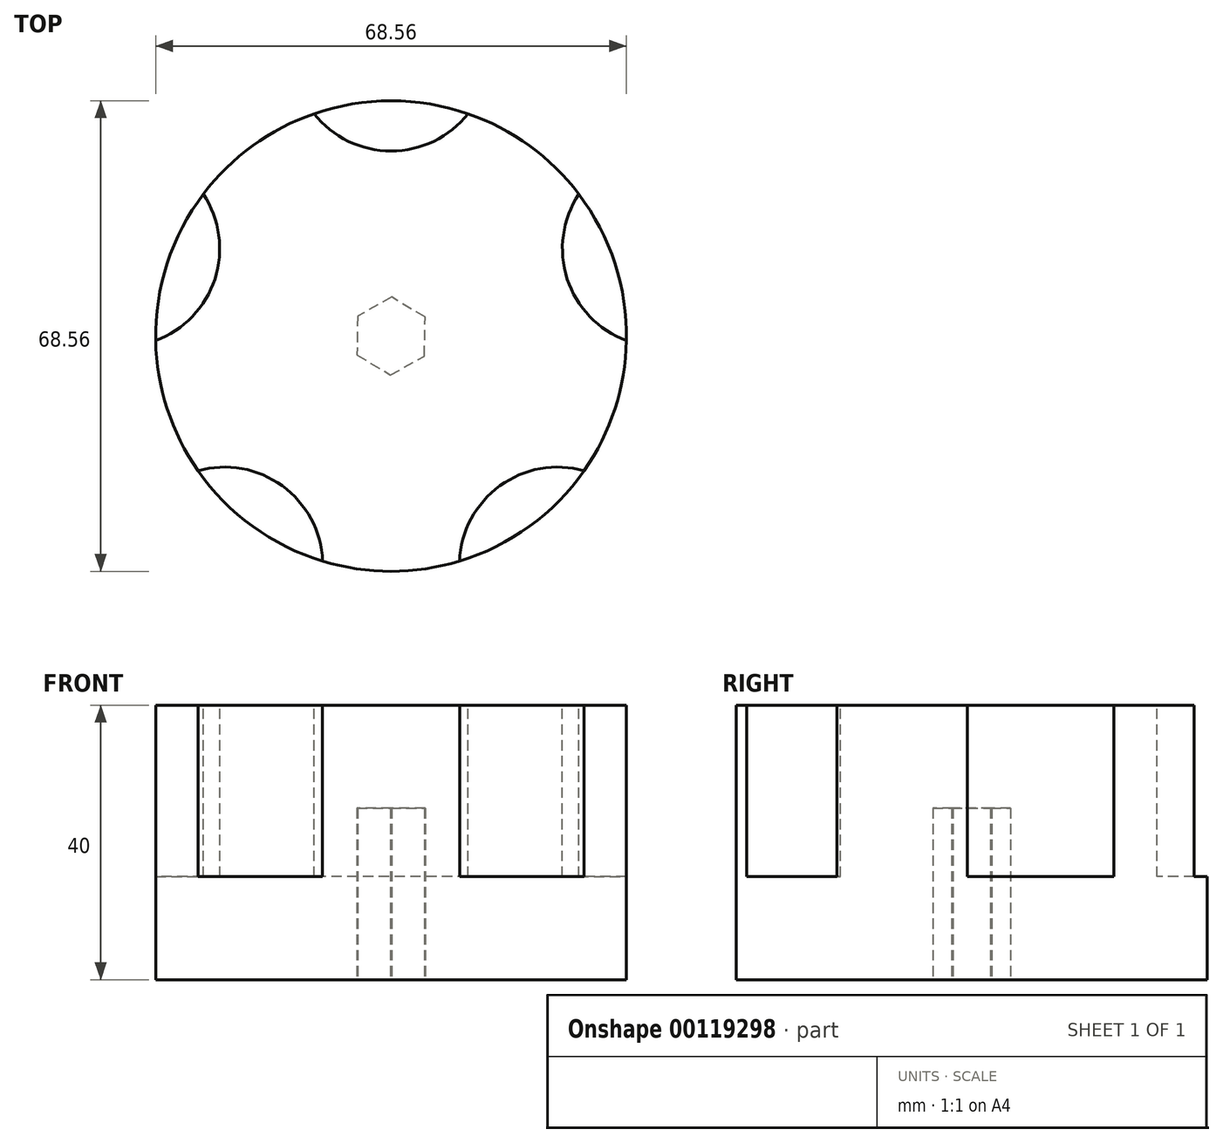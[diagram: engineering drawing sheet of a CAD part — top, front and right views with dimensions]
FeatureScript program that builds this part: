
annotation { "Feature Type Name" : "Feature", "Feature Type Description" : "" }
export const myFeature = defineFeature(function(context is Context, id is Id, definition is map)
    precondition{}
    {
        {
            var Q0;
            Q0=qCreatedBy(makeId("Top.planeOp"),FACE);
            var sketch = newSketch(context, id + "F0", { "sketchPlane" : qUnion([Q0])});
            skCircle(sketch, "E0", {"center": v(-24.43, 29.9) * mm, "radius": 34.28 * mm});
            skSolve(sketch);
        }
        {
            var Q0;
            Q0 = qSketchRegion(id + "F0", true);
            extrude(context, id + "F1", {"entities" : qUnion([Q0]), "depth" : 40 * mm});
        }
        {
            var Q0;
            Q0=makeQuery(id+"F1.opExtrude","CAP_FACE",FACE,{"disambiguationData":[OSD([sQuery(id+"F0.wireOp",EDGE,"E0")])],"isStart":false});
            var sketch = newSketch(context, id + "F2", { "sketchPlane" : qUnion([Q0])});
            skLineSegment(sketch, "E1", {"start": v(-24.43, 29.9) * mm, "end": v(-24.43, 71.17) * mm, "construction": true});
            skCircle(sketch, "E2", {"center": v(-24.43, 71.17) * mm, "radius": 14.3 * mm});
            skCircle(sketch, "E3.1.0", {"center": v(14.83, 42.65) * mm, "radius": 14.3 * mm});
            skCircle(sketch, "E3.2.0", {"center": v(-0.17, -3.49) * mm, "radius": 14.3 * mm});
            skCircle(sketch, "E3.3.0", {"center": v(-48.68, -3.49) * mm, "radius": 14.3 * mm});
            skCircle(sketch, "E3.4.0", {"center": v(-63.68, 42.65) * mm, "radius": 14.3 * mm});
            skPoint(sketch, "E3.center", {"position": v(-24.43, 29.9) * mm});
            skLineSegment(sketch, "E3.anchor2", {"start": v(-24.43, 29.9) * mm, "end": v(-63.68, 42.65) * mm, "construction": true});
            skSolve(sketch);
        }
        {
            var Q0;
            {var subQ0=sQuery(id+"F2.wireOp",EDGE,"E2");var subQ1=makeQuery(id+"F1.opExtrude","CAP_EDGE",EDGE,{"disambiguationData":[OSD([sQuery(id+"F0.wireOp",EDGE,"E0")])],"isStart":false});var subQ2=makeQuery(id+"F2.imprint","INTERSECT",VERTEX,{"disambiguationData":[OD(0.0)],"derivedFrom":[subQ1,subQ0]});Q0=makeQuery(id+"F2.imprint","IMPRINT",FACE,{"disambiguationData":[TD([[makeQuery(id+"F2.imprint","IMPRINT",EDGE,{"disambiguationData":[TD([[subQ2,-1.0]])],"derivedFrom":subQ0}),1.0]])]});}
            var Q1;
            {var subQ0=sQuery(id+"F2.wireOp",EDGE,"E2");var subQ1=makeQuery(id+"F1.opExtrude","CAP_EDGE",EDGE,{"disambiguationData":[OSD([sQuery(id+"F0.wireOp",EDGE,"E0")])],"isStart":false});var subQ2=makeQuery(id+"F2.imprint","INTERSECT",VERTEX,{"disambiguationData":[OD(0.0)],"derivedFrom":[subQ1,subQ0]});Q1=makeQuery(id+"F2.imprint","IMPRINT",FACE,{"disambiguationData":[TD([[makeQuery(id+"F2.imprint","IMPRINT",EDGE,{"disambiguationData":[TD([[subQ2,1.0]])],"derivedFrom":subQ0}),1.0]])]});}
            var Q2;
            {var subQ0=sQuery(id+"F2.wireOp",EDGE,"E3.1.0");var subQ1=makeQuery(id+"F1.opExtrude","CAP_EDGE",EDGE,{"disambiguationData":[OSD([sQuery(id+"F0.wireOp",EDGE,"E0")])],"isStart":false});var subQ2=makeQuery(id+"F2.imprint","INTERSECT",VERTEX,{"disambiguationData":[OD(0.0)],"derivedFrom":[subQ1,subQ0]});Q2=makeQuery(id+"F2.imprint","IMPRINT",FACE,{"disambiguationData":[TD([[makeQuery(id+"F2.imprint","IMPRINT",EDGE,{"disambiguationData":[TD([[subQ2,1.0]])],"derivedFrom":subQ0}),1.0]])]});}
            var Q3;
            {var subQ0=sQuery(id+"F2.wireOp",EDGE,"E3.1.0");var subQ1=makeQuery(id+"F1.opExtrude","CAP_EDGE",EDGE,{"disambiguationData":[OSD([sQuery(id+"F0.wireOp",EDGE,"E0")])],"isStart":false});var subQ2=makeQuery(id+"F2.imprint","INTERSECT",VERTEX,{"disambiguationData":[OD(0.0)],"derivedFrom":[subQ1,subQ0]});Q3=makeQuery(id+"F2.imprint","IMPRINT",FACE,{"disambiguationData":[TD([[makeQuery(id+"F2.imprint","IMPRINT",EDGE,{"disambiguationData":[TD([[subQ2,-1.0]])],"derivedFrom":subQ0}),1.0]])]});}
            var Q4;
            {var subQ0=sQuery(id+"F2.wireOp",EDGE,"E3.2.0");var subQ1=makeQuery(id+"F1.opExtrude","CAP_EDGE",EDGE,{"disambiguationData":[OSD([sQuery(id+"F0.wireOp",EDGE,"E0")])],"isStart":false});var subQ2=makeQuery(id+"F2.imprint","INTERSECT",VERTEX,{"disambiguationData":[OD(0.0)],"derivedFrom":[subQ1,subQ0]});Q4=makeQuery(id+"F2.imprint","IMPRINT",FACE,{"disambiguationData":[TD([[makeQuery(id+"F2.imprint","IMPRINT",EDGE,{"disambiguationData":[TD([[subQ2,1.0]])],"derivedFrom":subQ0}),1.0]])]});}
            var Q5;
            {var subQ0=sQuery(id+"F2.wireOp",EDGE,"E3.2.0");var subQ1=makeQuery(id+"F1.opExtrude","CAP_EDGE",EDGE,{"disambiguationData":[OSD([sQuery(id+"F0.wireOp",EDGE,"E0")])],"isStart":false});var subQ2=makeQuery(id+"F2.imprint","INTERSECT",VERTEX,{"disambiguationData":[OD(0.0)],"derivedFrom":[subQ1,subQ0]});Q5=makeQuery(id+"F2.imprint","IMPRINT",FACE,{"disambiguationData":[TD([[makeQuery(id+"F2.imprint","IMPRINT",EDGE,{"disambiguationData":[TD([[subQ2,-1.0]])],"derivedFrom":subQ0}),1.0]])]});}
            var Q6;
            {var subQ0=sQuery(id+"F2.wireOp",EDGE,"E3.3.0");var subQ1=makeQuery(id+"F1.opExtrude","CAP_EDGE",EDGE,{"disambiguationData":[OSD([sQuery(id+"F0.wireOp",EDGE,"E0")])],"isStart":false});var subQ2=makeQuery(id+"F2.imprint","INTERSECT",VERTEX,{"disambiguationData":[OD(0.0)],"derivedFrom":[subQ1,subQ0]});Q6=makeQuery(id+"F2.imprint","IMPRINT",FACE,{"disambiguationData":[TD([[makeQuery(id+"F2.imprint","IMPRINT",EDGE,{"disambiguationData":[TD([[subQ2,-1.0]])],"derivedFrom":subQ0}),1.0]])]});}
            var Q7;
            {var subQ0=sQuery(id+"F2.wireOp",EDGE,"E3.3.0");var subQ1=makeQuery(id+"F1.opExtrude","CAP_EDGE",EDGE,{"disambiguationData":[OSD([sQuery(id+"F0.wireOp",EDGE,"E0")])],"isStart":false});var subQ2=makeQuery(id+"F2.imprint","INTERSECT",VERTEX,{"disambiguationData":[OD(0.0)],"derivedFrom":[subQ1,subQ0]});Q7=makeQuery(id+"F2.imprint","IMPRINT",FACE,{"disambiguationData":[TD([[makeQuery(id+"F2.imprint","IMPRINT",EDGE,{"disambiguationData":[TD([[subQ2,1.0]])],"derivedFrom":subQ0}),1.0]])]});}
            var Q8;
            {var subQ0=sQuery(id+"F2.wireOp",EDGE,"E3.4.0");var subQ1=makeQuery(id+"F1.opExtrude","CAP_EDGE",EDGE,{"disambiguationData":[OSD([sQuery(id+"F0.wireOp",EDGE,"E0")])],"isStart":false});var subQ2=makeQuery(id+"F2.imprint","INTERSECT",VERTEX,{"disambiguationData":[OD(0.0)],"derivedFrom":[subQ1,subQ0]});Q8=makeQuery(id+"F2.imprint","IMPRINT",FACE,{"disambiguationData":[TD([[makeQuery(id+"F2.imprint","IMPRINT",EDGE,{"disambiguationData":[TD([[subQ2,1.0]])],"derivedFrom":subQ0}),1.0]])]});}
            var Q9;
            {var subQ0=sQuery(id+"F2.wireOp",EDGE,"E3.4.0");var subQ1=makeQuery(id+"F1.opExtrude","CAP_EDGE",EDGE,{"disambiguationData":[OSD([sQuery(id+"F0.wireOp",EDGE,"E0")])],"isStart":false});var subQ2=makeQuery(id+"F2.imprint","INTERSECT",VERTEX,{"disambiguationData":[OD(0.0)],"derivedFrom":[subQ1,subQ0]});Q9=makeQuery(id+"F2.imprint","IMPRINT",FACE,{"disambiguationData":[TD([[makeQuery(id+"F2.imprint","IMPRINT",EDGE,{"disambiguationData":[TD([[subQ2,-1.0]])],"derivedFrom":subQ0}),1.0]])]});}
            extrude(context, id + "F3", {"entities" : qUnion([Q0, Q1, Q2, Q3, Q4, Q5, Q6, Q7, Q8, Q9]), "operationType" : NewBodyOperationType.REMOVE, "oppositeDirection" : true, "depth" : 25 * mm});
        }
        {
            var Q0;
            Q0=makeQuery(id+"F1.opExtrude","CAP_FACE",FACE,{"disambiguationData":[OSD([sQuery(id+"F0.wireOp",EDGE,"E0")])],"isStart":true});
            var sketch = newSketch(context, id + "F4", { "sketchPlane" : qUnion([Q0])});
            skCircle(sketch, "E4.cCircle", {"center": v(-24.43, -29.9) * mm, "radius": 4.91 * mm, "construction": true});
            skLineSegment(sketch, "E4.0", {"start": v(-19.47, -32.65) * mm, "end": v(-24.33, -35.57) * mm});
            skLineSegment(sketch, "E4.1", {"start": v(-24.33, -35.57) * mm, "end": v(-29.29, -32.82) * mm});
            skLineSegment(sketch, "E4.2", {"start": v(-29.29, -32.82) * mm, "end": v(-29.38, -27.15) * mm});
            skLineSegment(sketch, "E4.3", {"start": v(-29.38, -27.15) * mm, "end": v(-24.52, -24.23) * mm});
            skLineSegment(sketch, "E4.4", {"start": v(-24.52, -24.23) * mm, "end": v(-19.56, -26.98) * mm});
            skLineSegment(sketch, "E4.5", {"start": v(-19.56, -26.98) * mm, "end": v(-19.47, -32.65) * mm});
            skPoint(sketch, "E4.0.midPoint", {"position": v(-21.9, -34.11) * mm});
            skSolve(sketch);
        }
        {
            var Q0;
            Q0=makeQuery(id+"F4.imprint","IMPRINT",FACE,{"disambiguationData":[TD([[makeQuery(id+"F4.imprint","IMPRINT",EDGE,{"derivedFrom":sQuery(id+"F4.wireOp",EDGE,"E4.0")}),-1.0]])]});
            extrude(context, id + "F5", {"entities" : qUnion([Q0]), "operationType" : NewBodyOperationType.REMOVE, "oppositeDirection" : true, "depth" : 25 * mm});
        }
    });
